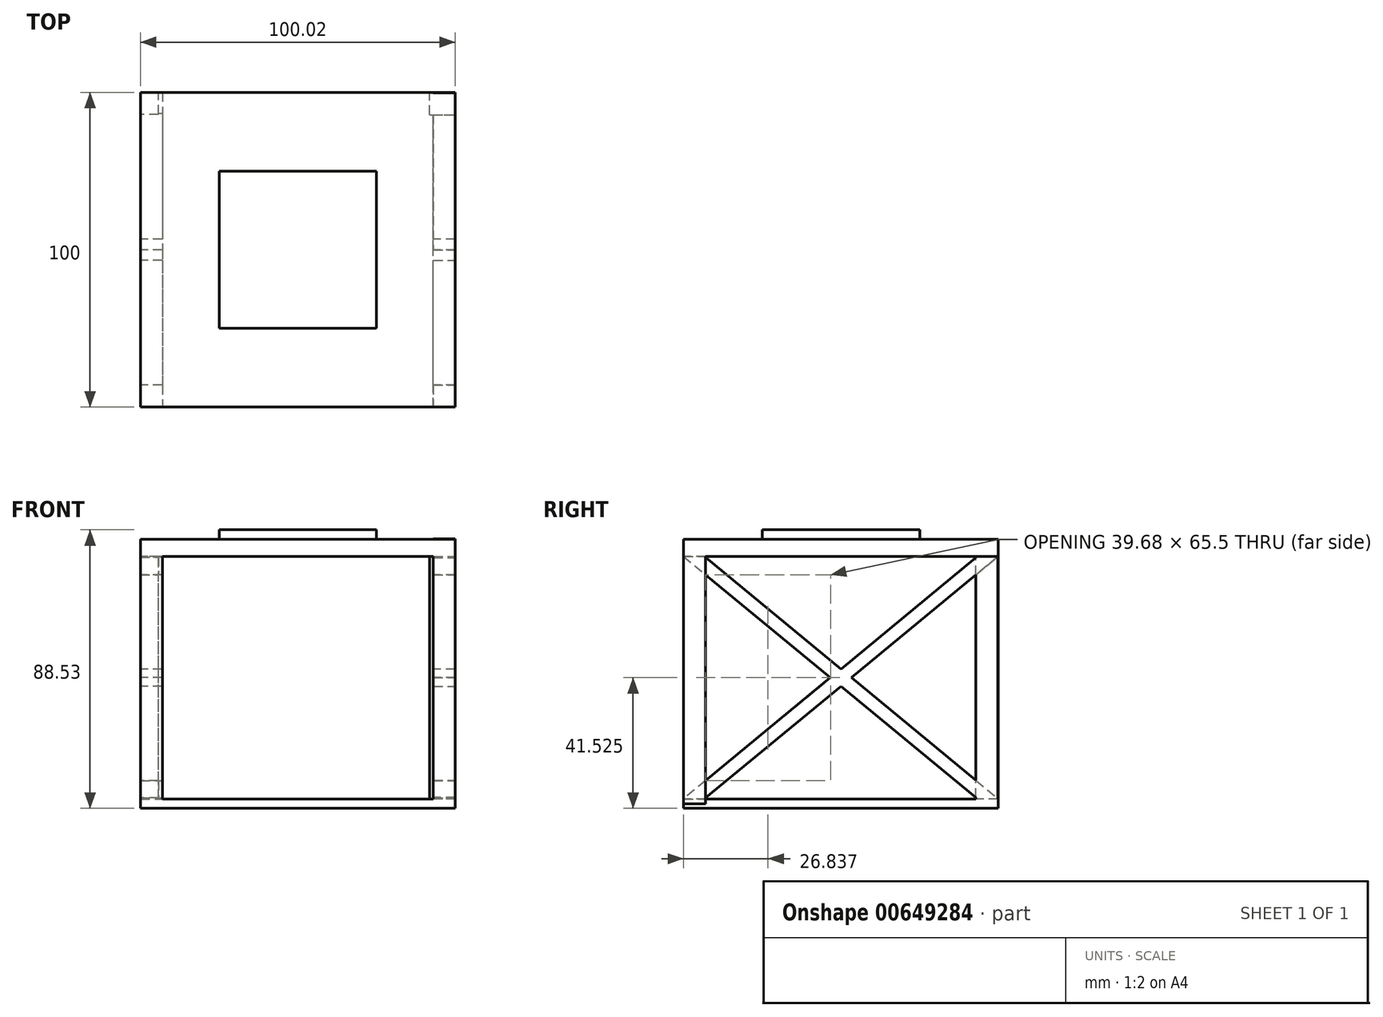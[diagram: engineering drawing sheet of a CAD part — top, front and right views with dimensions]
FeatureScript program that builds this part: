
annotation { "Feature Type Name" : "Feature", "Feature Type Description" : "" }
export const myFeature = defineFeature(function(context is Context, id is Id, definition is map)
    precondition{}
    {
        {
            var Q0;
            Q0=qCreatedBy(makeId("Top.planeOp"),FACE);
            var sketch = newSketch(context, id + "F0", { "sketchPlane" : qUnion([Q0])});
            skLineSegment(sketch, "E0.bottom", {"start": v(-44.37, 46.98) * mm, "end": v(55.63, 46.98) * mm});
            skLineSegment(sketch, "E0.top", {"start": v(-44.37, -53.02) * mm, "end": v(55.63, -53.02) * mm});
            skLineSegment(sketch, "E0.left", {"start": v(-44.37, 46.98) * mm, "end": v(-44.37, -53.02) * mm});
            skLineSegment(sketch, "E0.right", {"start": v(55.63, 46.98) * mm, "end": v(55.63, -53.02) * mm});
            skSolve(sketch);
        }
        {
            var Q0;
            Q0=qSketchRegion(id+"F0",true);
            extrude(context, id + "F1", {"entities" : qUnion([Q0]), "depth" : 3 * mm, "offsetDistance" : 25 * mm});
        }
        {
            var Q0;
            Q0=makeQuery(id+"F1.opExtrude","SWEPT_FACE",FACE,{"disambiguationData":[OSD([sQuery(id+"F0.wireOp",EDGE,"E0.left")])]});
            var sketch = newSketch(context, id + "F2", { "sketchPlane" : qUnion([Q0])});
            skLineSegment(sketch, "E1", {"start": v(-43.98, 0) * mm, "end": v(53.02, 80.05) * mm});
            skLineSegment(sketch, "E2", {"start": v(-46.98, 3) * mm, "end": v(53.02, 85.53) * mm});
            skLineSegment(sketch, "E3", {"start": v(-46.98, 3) * mm, "end": v(-46.98, 0) * mm});
            skLineSegment(sketch, "E4", {"start": v(-46.98, 0) * mm, "end": v(-43.98, 0) * mm});
            skLineSegment(sketch, "E5", {"start": v(53.02, 85.53) * mm, "end": v(53.02, 80.05) * mm});
            skSolve(sketch);
        }
        {
            var Q0;
            Q0=qSketchRegion(id+"F2",true);
            extrude(context, id + "F3", {"entities" : qUnion([Q0]), "operationType" : NewBodyOperationType.ADD, "oppositeDirection" : true, "depth" : 7 * mm, "offsetDistance" : 25 * mm});
        }
        {
            var Q0;
            Q0=makeQuery(id+"F3.boolean.opBoolean","MERGE",FACE,{"derivedFrom":[makeQuery(id+"F1.opExtrude","SWEPT_FACE",FACE,{"disambiguationData":[OSD([sQuery(id+"F0.wireOp",EDGE,"E0.left")])]}),makeQuery(id+"F3.opExtrude","CAP_FACE",FACE,{"disambiguationData":[OSD([sQuery(id+"F2.wireOp",EDGE,"E1"),sQuery(id+"F2.wireOp",EDGE,"E2"),sQuery(id+"F2.wireOp",EDGE,"E3"),sQuery(id+"F2.wireOp",EDGE,"E4"),sQuery(id+"F2.wireOp",EDGE,"E5")])],"isStart":true})]});
            var sketch = newSketch(context, id + "F4", { "sketchPlane" : qUnion([Q0])});
            skLineSegment(sketch, "E6", {"start": v(50.02, 0) * mm, "end": v(-46.98, 80.05) * mm});
            skLineSegment(sketch, "E7", {"start": v(53.02, 3) * mm, "end": v(-46.98, 85.53) * mm});
            skLineSegment(sketch, "E8", {"start": v(-46.98, 85.53) * mm, "end": v(-46.98, 80.05) * mm});
            skLineSegment(sketch, "E9", {"start": v(50.02, 0) * mm, "end": v(53.02, 0) * mm});
            skLineSegment(sketch, "E10", {"start": v(53.02, 0) * mm, "end": v(53.02, 3) * mm});
            skSolve(sketch);
        }
        {
            var Q0;
            Q0=qSketchRegion(id+"F4",true);
            extrude(context, id + "F5", {"entities" : qUnion([Q0]), "operationType" : NewBodyOperationType.ADD, "oppositeDirection" : true, "depth" : 7 * mm, "offsetDistance" : 25 * mm});
        }
        {
            var Q0;
            Q0=makeQuery(id+"F1.opExtrude","SWEPT_FACE",FACE,{"disambiguationData":[OSD([sQuery(id+"F0.wireOp",EDGE,"E0.right")])]});
            var sketch = newSketch(context, id + "F6", { "sketchPlane" : qUnion([Q0])});
            skLineSegment(sketch, "E11", {"start": v(-50.02, 0) * mm, "end": v(46.98, 80.05) * mm});
            skLineSegment(sketch, "E12", {"start": v(-50.02, 0) * mm, "end": v(-53.02, 0) * mm});
            skLineSegment(sketch, "E13", {"start": v(-53.02, 0) * mm, "end": v(-53.02, 3) * mm});
            skLineSegment(sketch, "E14", {"start": v(-53.02, 3) * mm, "end": v(46.98, 85.64) * mm});
            skLineSegment(sketch, "E15", {"start": v(46.98, 85.64) * mm, "end": v(46.98, 80.05) * mm});
            skSolve(sketch);
        }
        {
            var Q0;
            Q0=qSketchRegion(id+"F6",true);
            extrude(context, id + "F7", {"entities" : qUnion([Q0]), "operationType" : NewBodyOperationType.ADD, "oppositeDirection" : true, "depth" : 7 * mm, "offsetDistance" : 25 * mm});
        }
        {
            var Q0;
            Q0=makeQuery(id+"F7.boolean.opBoolean","MERGE",FACE,{"derivedFrom":[makeQuery(id+"F1.opExtrude","SWEPT_FACE",FACE,{"disambiguationData":[OSD([sQuery(id+"F0.wireOp",EDGE,"E0.right")])]}),makeQuery(id+"F7.opExtrude","CAP_FACE",FACE,{"disambiguationData":[OSD([sQuery(id+"F6.wireOp",EDGE,"E11"),sQuery(id+"F6.wireOp",EDGE,"E12"),sQuery(id+"F6.wireOp",EDGE,"E13"),sQuery(id+"F6.wireOp",EDGE,"E14"),sQuery(id+"F6.wireOp",EDGE,"E15")])],"isStart":true})]});
            var sketch = newSketch(context, id + "F8", { "sketchPlane" : qUnion([Q0])});
            skLineSegment(sketch, "E16", {"start": v(43.98, 0) * mm, "end": v(-53.02, 80.05) * mm});
            skLineSegment(sketch, "E17", {"start": v(-53.02, 80.05) * mm, "end": v(-53.02, 85.55) * mm});
            skLineSegment(sketch, "E18", {"start": v(-53.02, 85.55) * mm, "end": v(46.98, 3) * mm});
            skLineSegment(sketch, "E19", {"start": v(46.98, 3) * mm, "end": v(46.98, 0) * mm});
            skLineSegment(sketch, "E20", {"start": v(46.98, 0) * mm, "end": v(43.98, 0) * mm});
            skSolve(sketch);
        }
        {
            var Q0;
            Q0=qSketchRegion(id+"F8",true);
            extrude(context, id + "F9", {"entities" : qUnion([Q0]), "operationType" : NewBodyOperationType.ADD, "oppositeDirection" : true, "depth" : 7 * mm, "offsetDistance" : 25 * mm});
        }
        {
            var Q0;
            Q0=makeQuery(id+"F3.opExtrude","SWEPT_FACE",FACE,{"disambiguationData":[OSD([sQuery(id+"F2.wireOp",EDGE,"E5")])]});
            var sketch = newSketch(context, id + "F10", { "sketchPlane" : qUnion([Q0])});
            skLineSegment(sketch, "E21.bottom", {"start": v(-44.37, 85.53) * mm, "end": v(55.65, 85.53) * mm});
            skLineSegment(sketch, "E21.top", {"start": v(-44.37, 80.05) * mm, "end": v(55.65, 80.05) * mm});
            skLineSegment(sketch, "E21.left", {"start": v(-44.37, 85.53) * mm, "end": v(-44.37, 80.05) * mm});
            skLineSegment(sketch, "E21.right", {"start": v(55.65, 85.53) * mm, "end": v(55.65, 80.05) * mm});
            skSolve(sketch);
        }
        {
            var Q0;
            Q0=qSketchRegion(id+"F10",true);
            extrude(context, id + "F11", {"entities" : qUnion([Q0]), "operationType" : NewBodyOperationType.ADD, "oppositeDirection" : true, "depth" : 100 * mm, "offsetDistance" : 25 * mm});
        }
        {
            var Q0;
            Q0=makeQuery(id+"F11.opExtrude","SWEPT_FACE",FACE,{"disambiguationData":[OSD([sQuery(id+"F10.wireOp",EDGE,"E21.bottom")])]});
            var sketch = newSketch(context, id + "F12", { "sketchPlane" : qUnion([Q0])});
            skLineSegment(sketch, "E22.bottom", {"start": v(-19.37, 21.98) * mm, "end": v(30.63, 21.98) * mm});
            skLineSegment(sketch, "E22.top", {"start": v(-19.37, -28.02) * mm, "end": v(30.63, -28.02) * mm});
            skLineSegment(sketch, "E22.left", {"start": v(-19.37, 21.98) * mm, "end": v(-19.37, -28.02) * mm});
            skLineSegment(sketch, "E22.right", {"start": v(30.63, 21.98) * mm, "end": v(30.63, -28.02) * mm});
            skSolve(sketch);
        }
        {
            var Q0;
            Q0=qSketchRegion(id+"F12",true);
            extrude(context, id + "F13", {"entities" : qUnion([Q0]), "operationType" : NewBodyOperationType.ADD, "depth" : 3 * mm, "offsetDistance" : 25 * mm});
        }
        {
            var Q0;
            Q0=makeQuery(id+"F11.opExtrude","SWEPT_FACE",FACE,{"disambiguationData":[OSD([sQuery(id+"F10.wireOp",EDGE,"E21.bottom")])]});
            var sketch = newSketch(context, id + "F14", { "sketchPlane" : qUnion([Q0])});
            skLineSegment(sketch, "E23.bottom", {"start": v(-44.37, 46.98) * mm, "end": v(-38.58, 46.98) * mm});
            skLineSegment(sketch, "E23.top", {"start": v(-44.37, 39.98) * mm, "end": v(-38.58, 39.98) * mm});
            skLineSegment(sketch, "E23.left", {"start": v(-44.37, 46.98) * mm, "end": v(-44.37, 39.98) * mm});
            skLineSegment(sketch, "E23.right", {"start": v(-38.58, 46.98) * mm, "end": v(-38.58, 39.98) * mm});
            skLineSegment(sketch, "E24.bottom", {"start": v(55.63, 46.83) * mm, "end": v(47.43, 46.83) * mm});
            skLineSegment(sketch, "E24.top", {"start": v(55.63, 39.83) * mm, "end": v(47.43, 39.83) * mm});
            skLineSegment(sketch, "E24.left", {"start": v(55.63, 46.83) * mm, "end": v(55.63, 39.83) * mm});
            skLineSegment(sketch, "E24.right", {"start": v(47.43, 46.83) * mm, "end": v(47.43, 39.83) * mm});
            skLineSegment(sketch, "E25.bottom", {"start": v(55.65, -53.02) * mm, "end": v(48.65, -53.02) * mm});
            skLineSegment(sketch, "E25.top", {"start": v(55.65, -46.02) * mm, "end": v(48.65, -46.02) * mm});
            skLineSegment(sketch, "E25.left", {"start": v(55.65, -53.02) * mm, "end": v(55.65, -46.02) * mm});
            skLineSegment(sketch, "E25.right", {"start": v(48.65, -53.02) * mm, "end": v(48.65, -46.02) * mm});
            skLineSegment(sketch, "E26.bottom", {"start": v(-44.37, -53.02) * mm, "end": v(-37.37, -53.02) * mm});
            skLineSegment(sketch, "E26.top", {"start": v(-44.37, -46.02) * mm, "end": v(-37.37, -46.02) * mm});
            skLineSegment(sketch, "E26.left", {"start": v(-44.37, -53.02) * mm, "end": v(-44.37, -46.02) * mm});
            skLineSegment(sketch, "E26.right", {"start": v(-37.37, -53.02) * mm, "end": v(-37.37, -46.02) * mm});
            skSolve(sketch);
        }
        {
            var Q0;
            Q0 = qSketchRegion(id + "F14", true);
            extrude(context, id + "F15", {"entities" : qUnion([Q0]), "operationType" : NewBodyOperationType.ADD, "oppositeDirection" : true, "depth" : 84.1 * mm, "offsetDistance" : 25 * mm});
        }
    });
